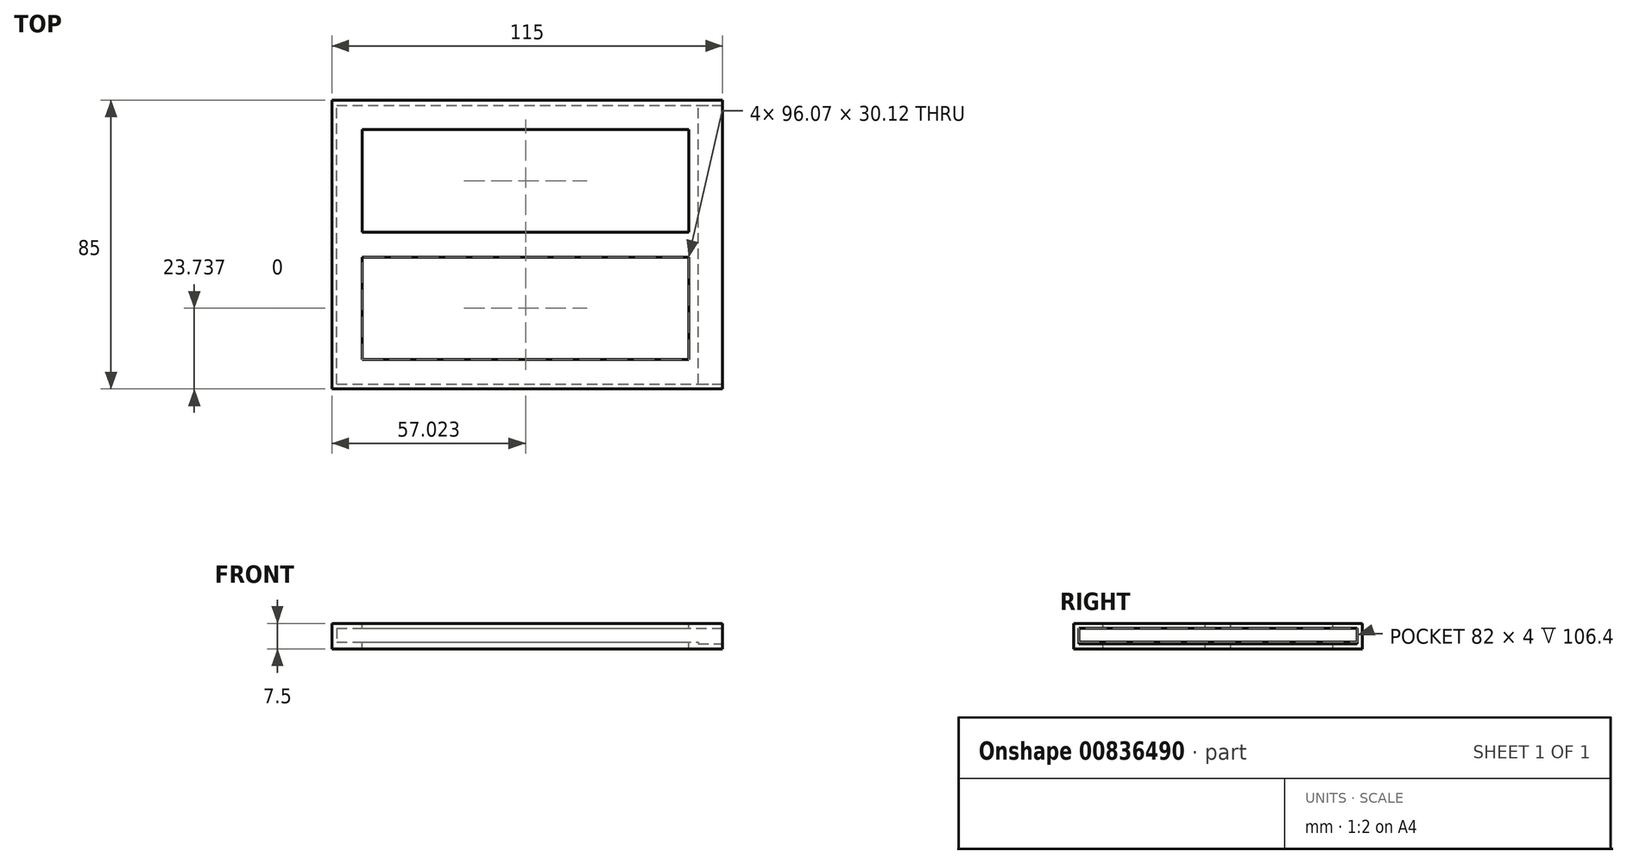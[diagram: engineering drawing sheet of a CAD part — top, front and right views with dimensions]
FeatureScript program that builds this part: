
annotation { "Feature Type Name" : "Feature", "Feature Type Description" : "" }
export const myFeature = defineFeature(function(context is Context, id is Id, definition is map)
    precondition{}
    {
        {
            var Q0;
            Q0=qCreatedBy(makeId("Top.planeOp"),FACE);
            var sketch = newSketch(context, id + "F0", { "sketchPlane" : qUnion([Q0])});
            skLineSegment(sketch, "E0.bottom", {"start": v(-40.3, -38.96) * mm, "end": v(74.7, -38.96) * mm});
            skLineSegment(sketch, "E0.top", {"start": v(-40.3, 46.04) * mm, "end": v(74.7, 46.04) * mm});
            skLineSegment(sketch, "E0.left", {"start": v(-40.3, -38.96) * mm, "end": v(-40.3, 46.04) * mm});
            skLineSegment(sketch, "E0.right", {"start": v(74.7, -38.96) * mm, "end": v(74.7, 46.04) * mm});
            skSolve(sketch);
        }
        {
            var Q0;
            Q0 = qSketchRegion(id + "F0", true);
            extrude(context, id + "F1", {"entities" : qUnion([Q0]), "depth" : 2 * mm, "offsetDistance" : 25 * mm});
        }
        {
            var Q0;
            Q0=makeQuery(id+"F1.opExtrude","CAP_FACE",FACE,{"disambiguationData":[OSD([sQuery(id+"F0.wireOp",EDGE,"E0.bottom"),sQuery(id+"F0.wireOp",EDGE,"E0.top"),sQuery(id+"F0.wireOp",EDGE,"E0.left"),sQuery(id+"F0.wireOp",EDGE,"E0.right")])],"isStart":false});
            var sketch = newSketch(context, id + "F2", { "sketchPlane" : qUnion([Q0])});
            skLineSegment(sketch, "E1.0", {"start": v(-38.8, -37.46) * mm, "end": v(-38.8, 44.54) * mm});
            skLineSegment(sketch, "E1.1", {"start": v(-38.8, -37.46) * mm, "end": v(73.2, -37.46) * mm});
            skLineSegment(sketch, "E1.2", {"start": v(73.2, -37.46) * mm, "end": v(73.2, 44.54) * mm});
            skLineSegment(sketch, "E1.3", {"start": v(-38.8, 44.54) * mm, "end": v(73.2, 44.54) * mm});
            skLineSegment(sketch, "E2.bottom", {"start": v(-40.3, -38.96) * mm, "end": v(74.7, -38.96) * mm});
            skLineSegment(sketch, "E2.top", {"start": v(-40.3, 46.04) * mm, "end": v(74.7, 46.04) * mm});
            skLineSegment(sketch, "E2.left", {"start": v(-40.3, -38.96) * mm, "end": v(-40.3, 46.04) * mm});
            skLineSegment(sketch, "E2.right", {"start": v(74.7, -38.96) * mm, "end": v(74.7, 46.04) * mm});
            skSolve(sketch);
        }
        {
            var Q0;
            Q0 = qSketchRegion(id + "F2", true);
            extrude(context, id + "F3", {"entities" : qUnion([Q0]), "operationType" : NewBodyOperationType.ADD, "depth" : 4 * mm, "offsetDistance" : 25 * mm});
        }
        {
            var Q0;
            Q0=makeQuery(id+"F3.opExtrude","CAP_FACE",FACE,{"disambiguationData":[OSD([sQuery(id+"F2.wireOp",EDGE,"E1.0"),sQuery(id+"F2.wireOp",EDGE,"E1.1"),sQuery(id+"F2.wireOp",EDGE,"E1.2"),sQuery(id+"F2.wireOp",EDGE,"E1.3"),sQuery(id+"F2.wireOp",EDGE,"E2.bottom"),sQuery(id+"F2.wireOp",EDGE,"E2.top"),sQuery(id+"F2.wireOp",EDGE,"E2.left"),sQuery(id+"F2.wireOp",EDGE,"E2.right")])],"isStart":false});
            var sketch = newSketch(context, id + "F4", { "sketchPlane" : qUnion([Q0])});
            skLineSegment(sketch, "E3.bottom", {"start": v(-40.3, -38.96) * mm, "end": v(74.7, -38.96) * mm});
            skLineSegment(sketch, "E3.top", {"start": v(-40.3, 46.04) * mm, "end": v(74.7, 46.04) * mm});
            skLineSegment(sketch, "E3.left", {"start": v(-40.3, -38.96) * mm, "end": v(-40.3, 46.04) * mm});
            skLineSegment(sketch, "E3.right", {"start": v(74.7, -38.96) * mm, "end": v(74.7, 46.04) * mm});
            skSolve(sketch);
        }
        {
            var Q0;
            Q0 = qSketchRegion(id + "F4", true);
            extrude(context, id + "F5", {"entities" : qUnion([Q0]), "operationType" : NewBodyOperationType.ADD, "depth" : 1.5 * mm, "offsetDistance" : 25 * mm});
        }
        {
            var Q0;
            Q0=makeQuery(id+"F5.boolean.opBoolean","MERGE",FACE,{"derivedFrom":[makeQuery(id+"F3.boolean.opBoolean","MERGE",FACE,{"derivedFrom":[makeQuery(id+"F1.opExtrude","SWEPT_FACE",FACE,{"disambiguationData":[OSD([sQuery(id+"F0.wireOp",EDGE,"E0.right")])]}),makeQuery(id+"F3.opExtrude","SWEPT_FACE",FACE,{"disambiguationData":[OSD([sQuery(id+"F2.wireOp",EDGE,"E2.right")])]})]}),makeQuery(id+"F5.opExtrude","SWEPT_FACE",FACE,{"disambiguationData":[OSD([sQuery(id+"F4.wireOp",EDGE,"E3.right")])]})]});
            var sketch = newSketch(context, id + "F6", { "sketchPlane" : qUnion([Q0])});
            skLineSegment(sketch, "E4.bottom", {"start": v(-37.46, 6) * mm, "end": v(44.54, 6) * mm});
            skLineSegment(sketch, "E4.top", {"start": v(-37.46, 1.5) * mm, "end": v(44.54, 1.5) * mm});
            skLineSegment(sketch, "E4.left", {"start": v(-37.46, 6) * mm, "end": v(-37.46, 1.5) * mm});
            skLineSegment(sketch, "E4.right", {"start": v(44.54, 6) * mm, "end": v(44.54, 1.5) * mm});
            skSolve(sketch);
        }
        {
            var Q0;
            Q0 = qSketchRegion(id + "F6", true);
            extrude(context, id + "F7", {"entities" : qUnion([Q0]), "operationType" : NewBodyOperationType.REMOVE, "oppositeDirection" : true, "depth" : 7.1 * mm, "offsetDistance" : 25 * mm});
        }
        {
            var Q0;
            Q0=makeQuery(id+"F5.opExtrude","CAP_FACE",FACE,{"disambiguationData":[OSD([sQuery(id+"F4.wireOp",EDGE,"E3.bottom"),sQuery(id+"F4.wireOp",EDGE,"E3.top"),sQuery(id+"F4.wireOp",EDGE,"E3.left"),sQuery(id+"F4.wireOp",EDGE,"E3.right")])],"isStart":false});
            var sketch = newSketch(context, id + "F8", { "sketchPlane" : qUnion([Q0])});
            skLineSegment(sketch, "E5.bottom", {"start": v(-31.31, 7.23) * mm, "end": v(64.76, 7.23) * mm});
            skLineSegment(sketch, "E5.top", {"start": v(-31.31, 37.36) * mm, "end": v(64.76, 37.36) * mm});
            skLineSegment(sketch, "E5.left", {"start": v(-31.31, 7.23) * mm, "end": v(-31.31, 37.36) * mm});
            skLineSegment(sketch, "E5.right", {"start": v(64.76, 7.23) * mm, "end": v(64.76, 37.36) * mm});
            skLineSegment(sketch, "E6.MirrorCS", {"start": v(-31.31, -0.16) * mm, "end": v(-31.31, -30.29) * mm});
            skLineSegment(sketch, "E7.MirrorCS", {"start": v(-31.31, -30.29) * mm, "end": v(64.76, -30.29) * mm});
            skLineSegment(sketch, "E8.MirrorCS", {"start": v(64.76, -0.16) * mm, "end": v(64.76, -30.29) * mm});
            skLineSegment(sketch, "E9.MirrorCS", {"start": v(-31.31, -0.16) * mm, "end": v(64.76, -0.16) * mm});
            skSolve(sketch);
        }
        {
            var Q0;
            Q0 = qSketchRegion(id + "F8", true);
            extrude(context, id + "F9", {"entities" : qUnion([Q0]), "operationType" : NewBodyOperationType.REMOVE, "oppositeDirection" : true, "depth" : 20 * mm, "offsetDistance" : 25 * mm});
        }
    });
